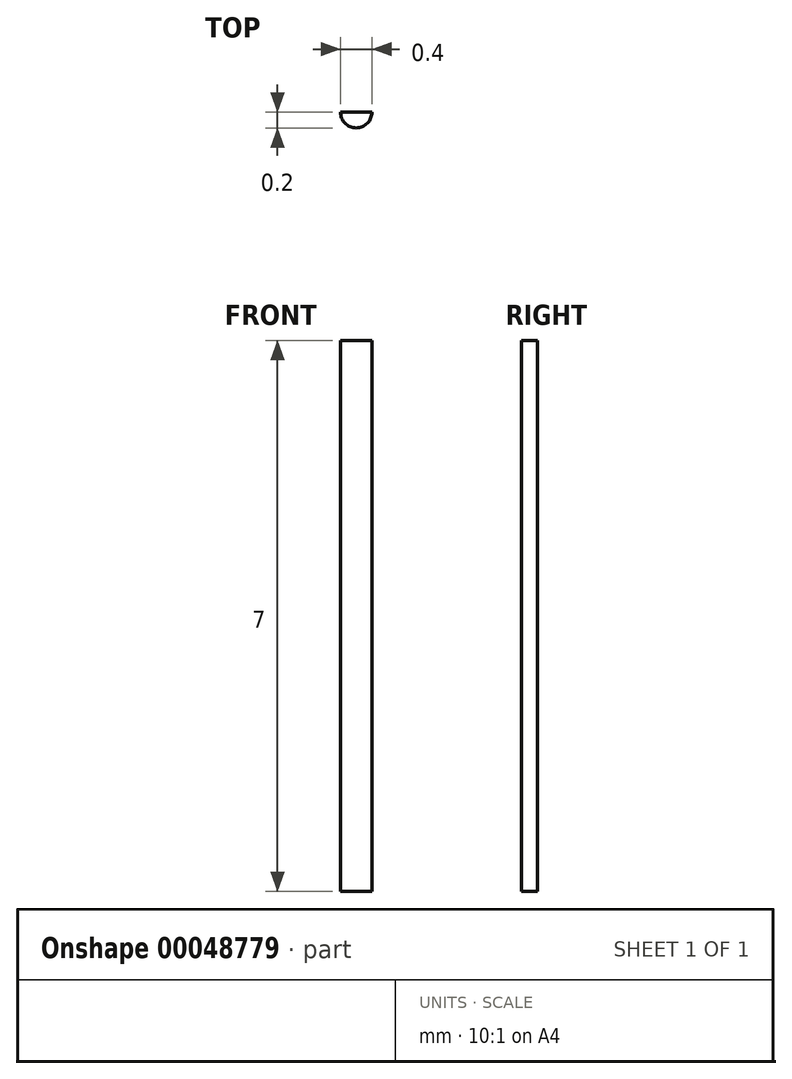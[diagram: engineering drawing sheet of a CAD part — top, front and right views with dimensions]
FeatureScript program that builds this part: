
annotation { "Feature Type Name" : "Feature", "Feature Type Description" : "" }
export const myFeature = defineFeature(function(context is Context, id is Id, definition is map)
    precondition{}
    {
        {
            var Q0;
            Q0=qCreatedBy(makeId("Front.planeOp"),FACE);
            var sketch = newSketch(context, id + "F0", { "sketchPlane" : qUnion([Q0])});
            skLineSegment(sketch, "E0.bottom", {"start": v(4.75, -3.5) * mm, "end": v(-4.75, -3.5) * mm});
            skLineSegment(sketch, "E0.top", {"start": v(4.75, 3.5) * mm, "end": v(-4.75, 3.5) * mm});
            skLineSegment(sketch, "E0.left", {"start": v(4.75, -3.5) * mm, "end": v(4.75, 3.5) * mm});
            skLineSegment(sketch, "E0.right", {"start": v(-4.75, -3.5) * mm, "end": v(-4.75, 3.5) * mm});
            skPoint(sketch, "E0.middle", {"position": v(0, 0) * mm});
            skSolve(sketch);
        }
        {
            var Q0;
            Q0=makeQuery(id+"F0.imprint","IMPRINT",FACE,{"disambiguationData":[TD([[makeQuery(id+"F0.imprint","IMPRINT",EDGE,{"derivedFrom":sQuery(id+"F0.wireOp",EDGE,"E0.bottom")}),-1.0]])]});
            extrude(context, id + "F1", {"entities" : qUnion([Q0]), "depth" : 1.1 * mm});
        }
        {
            var Q0;
            Q0=makeQuery(id+"F1.opExtrude","SWEPT_FACE",FACE,{"disambiguationData":[OSD([sQuery(id+"F0.wireOp",EDGE,"E0.bottom")])]});
            var sketch = newSketch(context, id + "F2", { "sketchPlane" : qUnion([Q0])});
            skArc(sketch, "E1", {"start": v(-0.2, 0) * mm, "mid": v(0, 0.2) * mm, "end": v(0.2, 0) * mm});
            skSolve(sketch);
        }
        {
            var Q0;
            {var subQ0=sQuery(id+"F2.wireOp",EDGE,"E1");Q0=makeQuery(id+"F2.imprint","IMPRINT",FACE,{"disambiguationData":[TD([[makeQuery(id+"F2.imprint","IMPRINT",EDGE,{"derivedFrom":subQ0}),-1.0]])]});}
            extrude(context, id + "F3", {"entities" : qUnion([Q0]), "operationType" : NewBodyOperationType.REMOVE, "endBound" : BoundingType.UP_TO_NEXT, "oppositeDirection" : true, "depth" : 25 * mm});
        }
    });
